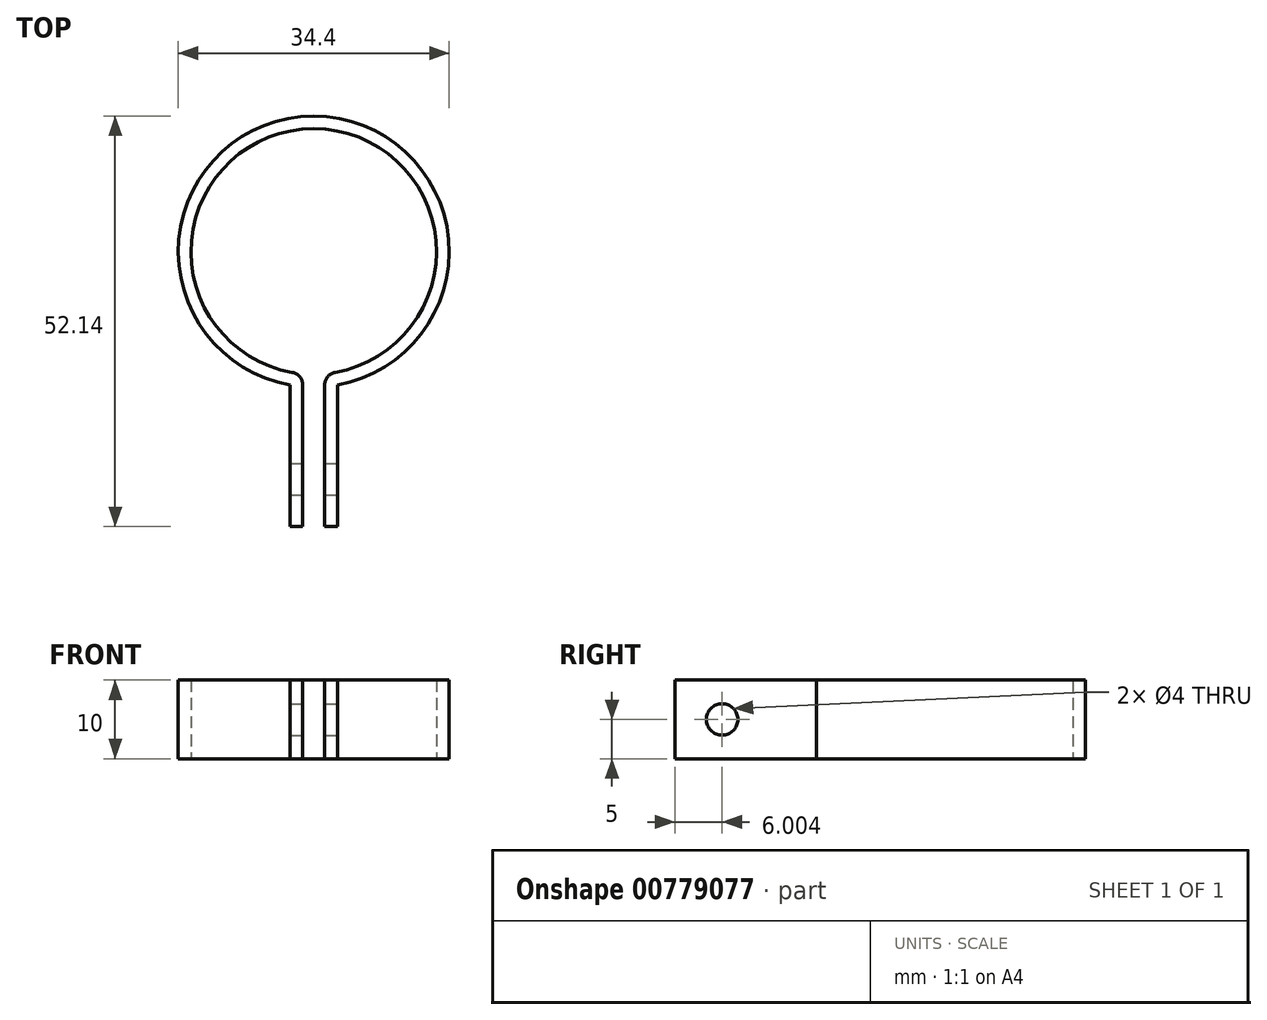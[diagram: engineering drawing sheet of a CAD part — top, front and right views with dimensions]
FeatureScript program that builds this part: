
annotation { "Feature Type Name" : "Feature", "Feature Type Description" : "" }
export const myFeature = defineFeature(function(context is Context, id is Id, definition is map)
    precondition{}
    {
        {
            var Q0;
            Q0=qCreatedBy(makeId("Top.planeOp"),FACE);
            var sketch = newSketch(context, id + "F0", { "sketchPlane" : qUnion([Q0])});
            skArc(sketch, "E0", {"start": v(2.72, -15.36) * mm, "mid": v(0, 15.6) * mm, "end": v(-2.72, -15.36) * mm});
            skArc(sketch, "E1.0", {"start": v(3, -16.94) * mm, "mid": v(0, 17.2) * mm, "end": v(-3, -16.94) * mm});
            skLineSegment(sketch, "E2", {"start": v(3, -16.94) * mm, "end": v(3, -34.94) * mm});
            skLineSegment(sketch, "E3", {"start": v(1.4, -16.94) * mm, "end": v(1.4, -34.94) * mm});
            skLineSegment(sketch, "E4", {"start": v(1.4, -34.94) * mm, "end": v(3, -34.94) * mm});
            skLineSegment(sketch, "E5.MirrorCS", {"start": v(-1.4, -16.94) * mm, "end": v(-1.4, -34.94) * mm});
            skLineSegment(sketch, "E6.MirrorCS", {"start": v(-3, -16.94) * mm, "end": v(-3, -34.94) * mm});
            skLineSegment(sketch, "E7.MirrorCS", {"start": v(-1.4, -34.94) * mm, "end": v(-3, -34.94) * mm});
            skPoint(sketch, "E8.visualSharp", {"position": v(-1.4, -15.54) * mm});
            skArc(sketch, "E8.filletArc", {"start": v(-1.4, -16.94) * mm, "mid": v(-1.77, -15.9) * mm, "end": v(-2.72, -15.36) * mm});
            skPoint(sketch, "E9.visualSharp", {"position": v(1.4, -15.54) * mm});
            skArc(sketch, "E9.filletArc", {"start": v(2.72, -15.36) * mm, "mid": v(1.77, -15.9) * mm, "end": v(1.4, -16.94) * mm});
            skSolve(sketch);
        }
        {
            var Q0;
            Q0 = qSketchRegion(id + "F0", true);
            extrude(context, id + "F1", {"entities" : qUnion([Q0]), "depth" : 10 * mm, "offsetDistance" : 25 * mm});
        }
        {
            var Q0;
            Q0=makeQuery(id+"F1.opExtrude","SWEPT_FACE",FACE,{"disambiguationData":[OSD([sQuery(id+"F0.wireOp",EDGE,"E2")])]});
            var sketch = newSketch(context, id + "F2", { "sketchPlane" : qUnion([Q0])});
            skCircle(sketch, "E10", {"center": v(-28.94, 5) * mm, "radius": 2 * mm});
            skLineSegment(sketch, "E11", {"start": v(-25.94, 12.37) * mm, "end": v(-25.94, -2.12) * mm, "construction": true});
            skPoint(sketch, "E11.startSnap0", {"position": v(-25.94, 10) * mm});
            skLineSegment(sketch, "E12", {"start": v(-16.94, 5) * mm, "end": v(-39.76, 5) * mm, "construction": true});
            skSolve(sketch);
        }
        {
            var Q0;
            Q0 = qSketchRegion(id + "F2", true);
            extrude(context, id + "F3", {"entities" : qUnion([Q0]), "operationType" : NewBodyOperationType.REMOVE, "oppositeDirection" : true, "depth" : 30 * mm, "offsetDistance" : 25 * mm});
        }
    });
